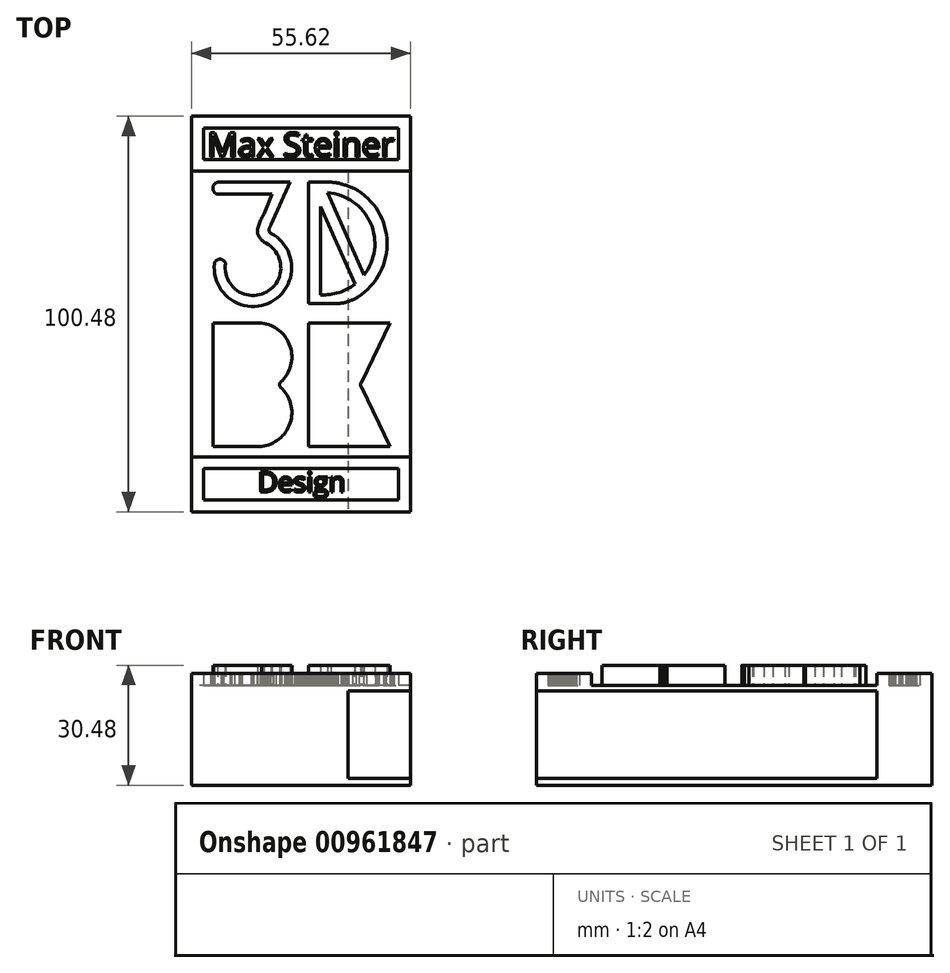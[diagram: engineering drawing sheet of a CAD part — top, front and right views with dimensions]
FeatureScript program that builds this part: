
annotation { "Feature Type Name" : "Feature", "Feature Type Description" : "" }
export const myFeature = defineFeature(function(context is Context, id is Id, definition is map)
    precondition{}
    {
        {
            var Q0;
            Q0=qCreatedBy(makeId("Top.planeOp"),FACE);
            var sketch = newSketch(context, id + "F0", { "sketchPlane" : qUnion([Q0])});
            skLineSegment(sketch, "E0", {"start": v(0, 56.35) * mm, "end": v(0, -56.35) * mm});
            skLineSegment(sketch, "E1", {"start": v(56.35, 0) * mm, "end": v(-56.35, 0) * mm});
            skPoint(sketch, "E2", {"position": v(0, 0) * mm});
            skPoint(sketch, "E3", {"position": v(-22.39, -33.62) * mm});
            skPoint(sketch, "E4", {"position": v(-22.39, 33.48) * mm});
            skPoint(sketch, "E5", {"position": v(21.85, 33.48) * mm});
            skLineSegment(sketch, "E6", {"start": v(1.95, 33.48) * mm, "end": v(7.67, 33.48) * mm});
            skLineSegment(sketch, "E7", {"start": v(21.85, -33.62) * mm, "end": v(1.95, -33.62) * mm});
            skLineSegment(sketch, "E8", {"start": v(21.85, 18.05) * mm, "end": v(21.85, 17.68) * mm});
            skLineSegment(sketch, "E9", {"start": v(-2.74, 33.48) * mm, "end": v(-21.16, 33.48) * mm});
            skLineSegment(sketch, "E10", {"start": v(-22.39, -33.62) * mm, "end": v(-10.07, -33.62) * mm});
            skLineSegment(sketch, "E11", {"start": v(-22.39, -2.3) * mm, "end": v(-22.39, -33.62) * mm});
            skPoint(sketch, "E12", {"position": v(-22.39, 31.95) * mm});
            skPoint(sketch, "E12.positionSnap0", {"position": v(-21.16, 31.95) * mm});
            skArc(sketch, "E13", {"start": v(-21.16, 33.48) * mm, "mid": v(-22.39, 31.95) * mm, "end": v(-21.16, 30.43) * mm});
            skPoint(sketch, "E14", {"position": v(-2.74, 33.48) * mm});
            skPoint(sketch, "E15", {"position": v(-7.3, 30.43) * mm});
            skLineSegment(sketch, "E16", {"start": v(-21.16, 30.43) * mm, "end": v(-7.3, 30.43) * mm});
            skPoint(sketch, "E17", {"position": v(-11.04, 20.68) * mm});
            skPoint(sketch, "E18", {"position": v(-9.45, 18.3) * mm});
            skPoint(sketch, "E19", {"position": v(-9.45, 25.39) * mm});
            skFitSpline(sketch, "E20", {"points": [v(-9.45, 25.39) * mm, v(-11.04, 20.68) * mm, v(-9.45, 18.3) * mm], "startDerivative": vector(-4.65, -9.06) * mm, "endDerivative": vector(5.1, -4.94) * mm});
            skLineSegment(sketch, "E21", {"start": v(-7.3, 30.43) * mm, "end": v(-9.45, 25.39) * mm});
            skPoint(sketch, "E22", {"position": v(-19.2, 12.85) * mm});
            skPoint(sketch, "E23", {"position": v(-12.14, 4.7) * mm});
            skArc(sketch, "E24", {"start": v(-19.2, 12.85) * mm, "mid": v(-8.74, 5.6) * mm, "end": v(-9.45, 18.3) * mm});
            skPoint(sketch, "E25", {"position": v(-8.14, 21.15) * mm});
            skPoint(sketch, "E26", {"position": v(-7.55, 20.43) * mm});
            skPoint(sketch, "E27", {"position": v(-7.55, 22.7) * mm});
            skFitSpline(sketch, "E28", {"points": [v(-7.55, 22.7) * mm, v(-8.14, 21.15) * mm, v(-7.55, 20.43) * mm], "startDerivative": vector(-1.74, -3) * mm, "endDerivative": vector(1.9, -1.47) * mm});
            skLineSegment(sketch, "E29", {"start": v(-2.74, 33.48) * mm, "end": v(-7.55, 22.7) * mm});
            skArc(sketch, "E30.0", {"start": v(-21.98, 12.85) * mm, "mid": v(-7.57, 3.08) * mm, "end": v(-7.62, 20.5) * mm});
            skPoint(sketch, "E31", {"position": v(-21.98, 12.85) * mm});
            skPoint(sketch, "E32", {"position": v(-20.63, 13.93) * mm});
            skArc(sketch, "E33", {"start": v(-19.2, 12.85) * mm, "mid": v(-20.59, 13.94) * mm, "end": v(-21.98, 12.85) * mm});
            skLineSegment(sketch, "E34", {"start": v(1.95, 33.48) * mm, "end": v(1.95, 2.25) * mm});
            skPoint(sketch, "E35", {"position": v(21.85, 18.05) * mm});
            skArc(sketch, "E36", {"start": v(13.56, 3.8) * mm, "mid": v(21.85, 17.87) * mm, "end": v(13.56, 31.93) * mm});
            skPoint(sketch, "E37", {"position": v(7.67, 33.48) * mm});
            skPoint(sketch, "E38", {"position": v(13.56, 31.93) * mm});
            skPoint(sketch, "E39", {"position": v(13.56, 3.8) * mm});
            skArc(sketch, "E40.0", {"start": v(5.03, 4.88) * mm, "mid": v(9.62, 5.44) * mm, "end": v(13.73, 7.58) * mm});
            skLineSegment(sketch, "E40.1", {"start": v(5.03, 27.26) * mm, "end": v(5.03, 4.88) * mm});
            skLineSegment(sketch, "E41", {"start": v(5.03, 27.26) * mm, "end": v(13.73, 7.58) * mm});
            skLineSegment(sketch, "E42", {"start": v(16.04, 9.89) * mm, "end": v(6.78, 30.83) * mm});
            skLineSegment(sketch, "E43", {"start": v(-22.39, -2.3) * mm, "end": v(-10.07, -2.3) * mm});
            skLineSegment(sketch, "E44", {"start": v(1.95, -2.3) * mm, "end": v(1.95, -33.62) * mm});
            skLineSegment(sketch, "E45", {"start": v(1.95, -2.3) * mm, "end": v(22.67, -2.3) * mm});
            skLineSegment(sketch, "E46", {"start": v(22.67, -2.3) * mm, "end": v(15.49, -17.1) * mm});
            skFitSpline(sketch, "E47", {"points": [v(15.49, -17.1) * mm, v(15.2, -17.6) * mm, v(15.17, -17.96) * mm], "startDerivative": vector(-0.63, -0.9) * mm, "endDerivative": vector(0.03, -0.82) * mm});
            skLineSegment(sketch, "E48.MirrorCS", {"start": v(1.95, -33.62) * mm, "end": v(22.67, -33.62) * mm});
            skLineSegment(sketch, "E49.MirrorCS", {"start": v(22.67, -33.62) * mm, "end": v(15.49, -18.82) * mm});
            skFitSpline(sketch, "E50.MirrorCS", {"points": [v(15.49, -18.82) * mm, v(15.2, -18.34) * mm, v(15.17, -17.96) * mm], "startDerivative": vector(-0.63, 0.9) * mm, "endDerivative": vector(0.03, 0.82) * mm});
            skArc(sketch, "E51", {"start": v(-5.17, -17.31) * mm, "mid": v(-2.75, -8.22) * mm, "end": v(-10.07, -2.3) * mm});
            skFitSpline(sketch, "E52", {"points": [v(-5.17, -17.31) * mm, v(-5.38, -17.68) * mm, v(-5.4, -17.96) * mm], "startDerivative": vector(-0.48, -0.68) * mm, "endDerivative": vector(0.02, -0.62) * mm});
            skArc(sketch, "E53.MirrorCS", {"start": v(-5.17, -18.61) * mm, "mid": v(-2.75, -27.7) * mm, "end": v(-10.07, -33.62) * mm});
            skFitSpline(sketch, "E54.MirrorCS", {"points": [v(-5.17, -18.61) * mm, v(-5.38, -18.25) * mm, v(-5.4, -17.96) * mm], "startDerivative": vector(-0.48, 0.68) * mm, "endDerivative": vector(0.02, 0.62) * mm});
            skPoint(sketch, "E55.end.orphan", {"position": v(-10.07, -33.62) * mm});
            skPoint(sketch, "E56.orphan", {"position": v(-10.07, -17.96) * mm});
            skPoint(sketch, "E57.orphan", {"position": v(0, -33.62) * mm});
            skLineSegment(sketch, "E58.MirrorCS", {"start": v(0, 2.62) * mm, "end": v(7.67, 2.62) * mm});
            skArc(sketch, "E59.trimOffspring", {"start": v(16.04, 9.89) * mm, "mid": v(17.67, 23.12) * mm, "end": v(6.78, 30.83) * mm});
            skPoint(sketch, "E60", {"position": v(7.67, 2.62) * mm});
            skFitSpline(sketch, "E61", {"points": [v(13.56, 3.8) * mm, v(10.55, 2.81) * mm, v(7.67, 2.62) * mm], "startDerivative": vector(-5.9, -2.33) * mm, "endDerivative": vector(-5.9, -0.02) * mm});
            skPoint(sketch, "E62.1.internal.snap0", {"position": v(9.38, 17.42) * mm});
            skFitSpline(sketch, "E62", {"points": [v(13.56, 31.93) * mm, v(9.38, 33.27) * mm, v(7.67, 33.48) * mm], "startDerivative": vector(-7.54, 2.7) * mm, "endDerivative": vector(-3.99, 0.22) * mm});
            skPoint(sketch, "E63.orphan", {"position": v(10.87, 2.62) * mm});
            skPoint(sketch, "E64.orphan", {"position": v(0, 33.48) * mm});
            skPoint(sketch, "E65.trimOffspring.start.orphan", {"position": v(21.85, 2.62) * mm});
            skLineSegment(sketch, "E66", {"start": v(-27.8, 0) * mm, "end": v(-27.8, 46.45) * mm});
            skLineSegment(sketch, "E67", {"start": v(-27.8, 46.45) * mm, "end": v(0, 46.45) * mm});
            skLineSegment(sketch, "E68.MirrorCS", {"start": v(27.8, 0) * mm, "end": v(27.8, 46.45) * mm});
            skLineSegment(sketch, "E69.MirrorCS", {"start": v(-27.8, -46.45) * mm, "end": v(0, -46.45) * mm});
            skLineSegment(sketch, "E70.MirrorCS", {"start": v(-27.8, 0) * mm, "end": v(-27.8, -46.45) * mm});
            skLineSegment(sketch, "E71.MirrorCS", {"start": v(27.8, 46.45) * mm, "end": v(0, 46.45) * mm});
            skLineSegment(sketch, "E72.MirrorCS", {"start": v(27.8, 0) * mm, "end": v(27.8, -46.45) * mm});
            skLineSegment(sketch, "E73.MirrorCS", {"start": v(27.8, -46.45) * mm, "end": v(0, -46.45) * mm});
            skSolve(sketch);
        }
        {
            var Q0;
            Q0=qCreatedBy(makeId("Top.planeOp"),FACE);
            var sketch = newSketch(context, id + "F1", { "sketchPlane" : qUnion([Q0])});
            skLineSegment(sketch, "E74.bottom", {"start": v(-27.8, 46.45) * mm, "end": v(27.8, 46.45) * mm});
            skLineSegment(sketch, "E74.top", {"start": v(-27.8, -46.45) * mm, "end": v(27.8, -46.45) * mm});
            skLineSegment(sketch, "E74.left", {"start": v(-27.8, 46.45) * mm, "end": v(-27.8, -46.45) * mm});
            skLineSegment(sketch, "E74.right", {"start": v(27.8, 46.45) * mm, "end": v(27.8, -46.45) * mm});
            skSolve(sketch);
        }
        {
            var Q0;
            Q0=makeQuery(id+"F1.imprint","IMPRINT",FACE,{"disambiguationData":[TD([[makeQuery(id+"F1.imprint","IMPRINT",EDGE,{"derivedFrom":sQuery(id+"F1.wireOp",EDGE,"E74.bottom")}),-1.0]])]});
            extrude(context, id + "F2", {"entities" : qUnion([Q0]), "oppositeDirection" : true, "depth" : 25.4 * mm, "offsetDistance" : 25.4 * mm});
        }
        {
            var Q0;
            {var subQ7=sQuery(id+"F0.wireOp",EDGE,"E6");Q0=makeQuery(id+"F0.imprint","IMPRINT",FACE,{"disambiguationData":[TD([[makeQuery(id+"F0.imprint","IMPRINT",EDGE,{"derivedFrom":subQ7}),-1.0]])]});}
            var Q1;
            Q1=makeQuery(id+"F0.imprint","IMPRINT",FACE,{"disambiguationData":[TD([[makeQuery(id+"F0.imprint","IMPRINT",EDGE,{"derivedFrom":sQuery(id+"F0.wireOp",EDGE,"E9")}),1.0]])]});
            var Q2;
            {var subQ0=sQuery(id+"F0.wireOp",EDGE,"E44");Q2=makeQuery(id+"F0.imprint","IMPRINT",FACE,{"disambiguationData":[TD([[makeQuery(id+"F0.imprint","IMPRINT",EDGE,{"derivedFrom":subQ0}),1.0]])]});}
            var Q3;
            Q3=makeQuery(id+"F0.imprint","IMPRINT",FACE,{"disambiguationData":[TD([[makeQuery(id+"F0.imprint","IMPRINT",EDGE,{"derivedFrom":sQuery(id+"F0.wireOp",EDGE,"E10")}),1.0]])]});
            extrude(context, id + "F3", {"entities" : qUnion([Q0, Q1, Q2, Q3]), "operationType" : NewBodyOperationType.ADD, "depth" : 5.08 * mm, "offsetDistance" : 25.4 * mm});
        }
        {
            var Q0;
            {var subQ3=sQuery(id+"F1.wireOp",EDGE,"E74.bottom");var subQ5=sQuery(id+"F1.wireOp",EDGE,"E74.left");var subQ6=sQuery(id+"F1.wireOp",EDGE,"E74.top");var subQ7=sQuery(id+"F1.wireOp",EDGE,"E74.right");Q0=makeQuery(id+"F3.boolean.opBoolean","SPLIT",FACE,{"disambiguationData":[TD([makeQuery(id+"F2.opExtrude","SWEPT_FACE",FACE,{"disambiguationData":[OSD([subQ3])]})])],"derivedFrom":makeQuery(id+"F2.opExtrude","CAP_FACE",FACE,{"disambiguationData":[OSD([subQ3,subQ6,subQ5,subQ7])],"isStart":true})});}
            var sketch = newSketch(context, id + "F4", { "sketchPlane" : qUnion([Q0])});
            skLineSegment(sketch, "E75", {"start": v(-27.8, 36.27) * mm, "end": v(27.8, 36.27) * mm});
            skLineSegment(sketch, "E76", {"start": v(-27.8, 36.27) * mm, "end": v(-27.8, 50.24) * mm});
            skLineSegment(sketch, "E77", {"start": v(-27.8, 50.24) * mm, "end": v(27.8, 50.24) * mm});
            skLineSegment(sketch, "E78", {"start": v(27.8, 50.24) * mm, "end": v(27.8, 36.27) * mm});
            skLineSegment(sketch, "E79.0", {"start": v(-24.8, 47.24) * mm, "end": v(24.8, 47.24) * mm});
            skLineSegment(sketch, "E79.1", {"start": v(-24.8, 39.27) * mm, "end": v(-24.8, 47.24) * mm});
            skLineSegment(sketch, "E79.2", {"start": v(-24.8, 39.27) * mm, "end": v(24.8, 39.27) * mm});
            skLineSegment(sketch, "E79.3", {"start": v(24.8, 47.24) * mm, "end": v(24.8, 39.27) * mm});
            skText(sketch, "E80", { "text": "Max Steiner", "fontName": "OpenSans-Regular.ttf"});
            skLineSegment(sketch, "E81", {"start": v(0, 0) * mm, "end": v(41.07, 0) * mm});
            skLineSegment(sketch, "E82.MirrorCS", {"start": v(-27.8, -50.24) * mm, "end": v(27.8, -50.24) * mm});
            skLineSegment(sketch, "E83.MirrorCS", {"start": v(-27.8, -36.27) * mm, "end": v(-27.8, -50.24) * mm});
            skLineSegment(sketch, "E84.MirrorCS", {"start": v(27.8, -50.24) * mm, "end": v(27.8, -36.27) * mm});
            skLineSegment(sketch, "E85.MirrorCS", {"start": v(-24.8, -39.27) * mm, "end": v(24.8, -39.27) * mm});
            skLineSegment(sketch, "E86.MirrorCS", {"start": v(-24.8, -39.27) * mm, "end": v(-24.8, -47.24) * mm});
            skLineSegment(sketch, "E87.MirrorCS", {"start": v(-24.8, -47.24) * mm, "end": v(24.8, -47.24) * mm});
            skLineSegment(sketch, "E88.MirrorCS", {"start": v(24.8, -47.24) * mm, "end": v(24.8, -39.27) * mm});
            skText(sketch, "E89", { "text": "Design", "fontName": "OpenSans-Regular.ttf"});
            skPoint(sketch, "E90", {"position": v(0, -39.27) * mm});
            skPoint(sketch, "E91", {"position": v(24.8, -43.26) * mm});
            skLineSegment(sketch, "E92", {"start": v(27.8, -36.27) * mm, "end": v(-27.8, -36.27) * mm});
            const initialGuessF4  = {"E80": [-0.02384, 0.03994, 1, 0, 0.00618], "E89": [-0.011, -0.04517, 1, 0, 0.00504]};
            skSetInitialGuess(sketch, initialGuessF4);
            skSolve(sketch);
        }
        {
            var Q0;
            Q0=makeQuery(id+"F4.imprint","IMPRINT",FACE,{"disambiguationData":[TD([[makeQuery(id+"F4.imprint","IMPRINT",EDGE,{"derivedFrom":sQuery(id+"F4.wireOp",EDGE,"E80.sketch_text.stroke-18")}),-1.0]])]});
            var Q1;
            Q1=makeQuery(id+"F4.imprint","IMPRINT",FACE,{"disambiguationData":[TD([[makeQuery(id+"F4.imprint","IMPRINT",EDGE,{"derivedFrom":sQuery(id+"F4.wireOp",EDGE,"E80.sketch_text.stroke-0")}),-1.0]])]});
            var Q2;
            Q2=makeQuery(id+"F4.imprint","IMPRINT",FACE,{"disambiguationData":[TD([[makeQuery(id+"F4.imprint","IMPRINT",EDGE,{"derivedFrom":sQuery(id+"F4.wireOp",EDGE,"E80.sketch_text.stroke-45")}),-1.0]])]});
            var Q3;
            Q3=makeQuery(id+"F4.imprint","IMPRINT",FACE,{"disambiguationData":[TD([[makeQuery(id+"F4.imprint","IMPRINT",EDGE,{"derivedFrom":sQuery(id+"F4.wireOp",EDGE,"E80.sketch_text.stroke-57")}),-1.0]])]});
            var Q4;
            Q4=makeQuery(id+"F4.imprint","IMPRINT",FACE,{"disambiguationData":[TD([[makeQuery(id+"F4.imprint","IMPRINT",EDGE,{"derivedFrom":sQuery(id+"F4.wireOp",EDGE,"E80.sketch_text.stroke-82")}),-1.0]])]});
            var Q5;
            Q5=makeQuery(id+"F4.imprint","IMPRINT",FACE,{"disambiguationData":[TD([[makeQuery(id+"F4.imprint","IMPRINT",EDGE,{"derivedFrom":sQuery(id+"F4.wireOp",EDGE,"E80.sketch_text.stroke-101")}),-1.0]])]});
            var Q6;
            Q6=makeQuery(id+"F4.imprint","IMPRINT",FACE,{"disambiguationData":[TD([[makeQuery(id+"F4.imprint","IMPRINT",EDGE,{"derivedFrom":sQuery(id+"F4.wireOp",EDGE,"E80.sketch_text.stroke-120")}),-1.0]])]});
            var Q7;
            Q7=makeQuery(id+"F4.imprint","IMPRINT",FACE,{"disambiguationData":[TD([[makeQuery(id+"F4.imprint","IMPRINT",EDGE,{"derivedFrom":sQuery(id+"F4.wireOp",EDGE,"E80.sketch_text.stroke-124")}),-1.0]])]});
            var Q8;
            Q8=makeQuery(id+"F4.imprint","IMPRINT",FACE,{"disambiguationData":[TD([[makeQuery(id+"F4.imprint","IMPRINT",EDGE,{"derivedFrom":sQuery(id+"F4.wireOp",EDGE,"E80.sketch_text.stroke-132")}),-1.0]])]});
            var Q9;
            Q9=makeQuery(id+"F4.imprint","IMPRINT",FACE,{"disambiguationData":[TD([[makeQuery(id+"F4.imprint","IMPRINT",EDGE,{"derivedFrom":sQuery(id+"F4.wireOp",EDGE,"E80.sketch_text.stroke-149")}),-1.0]])]});
            var Q10;
            Q10=makeQuery(id+"F4.imprint","IMPRINT",FACE,{"disambiguationData":[TD([[makeQuery(id+"F4.imprint","IMPRINT",EDGE,{"derivedFrom":sQuery(id+"F4.wireOp",EDGE,"E80.sketch_text.stroke-168")}),-1.0]])]});
            var Q11;
            {var subQ0=sQuery(id+"F4.wireOp",EDGE,"E76");Q11=makeQuery(id+"F4.imprint","IMPRINT",FACE,{"disambiguationData":[TD([[makeQuery(id+"F4.imprint","IMPRINT",EDGE,{"derivedFrom":subQ0}),1.0]])]});}
            var Q12;
            {var subQ2=sQuery(id+"F4.wireOp",EDGE,"E77");Q12=makeQuery(id+"F4.imprint","IMPRINT",FACE,{"disambiguationData":[TD([[makeQuery(id+"F4.imprint","IMPRINT",EDGE,{"derivedFrom":subQ2}),-1.0]])]});}
            extrude(context, id + "F5", {"entities" : qUnion([Q0, Q1, Q2, Q3, Q4, Q5, Q6, Q7, Q8, Q9, Q10, Q11, Q12]), "operationType" : NewBodyOperationType.ADD, "depth" : 3 * mm, "offsetDistance" : 25.4 * mm});
        }
        {
            var Q0;
            {var subQ1=sQuery(id+"F4.wireOp",EDGE,"E85.MirrorCS");Q0=makeQuery(id+"F4.imprint","IMPRINT",FACE,{"disambiguationData":[TD([[makeQuery(id+"F4.imprint","IMPRINT",EDGE,{"derivedFrom":subQ1}),1.0]])]});}
            var Q1;
            {var subQ8=sQuery(id+"F4.wireOp",EDGE,"E82.MirrorCS");Q1=makeQuery(id+"F4.imprint","IMPRINT",FACE,{"disambiguationData":[TD([[makeQuery(id+"F4.imprint","IMPRINT",EDGE,{"derivedFrom":subQ8}),1.0]])]});}
            var Q2;
            Q2=makeQuery(id+"F4.imprint","IMPRINT",FACE,{"disambiguationData":[TD([[makeQuery(id+"F4.imprint","IMPRINT",EDGE,{"derivedFrom":sQuery(id+"F4.wireOp",EDGE,"E89.sketch_text.stroke-0")}),-1.0]])]});
            var Q3;
            Q3=makeQuery(id+"F4.imprint","IMPRINT",FACE,{"disambiguationData":[TD([[makeQuery(id+"F4.imprint","IMPRINT",EDGE,{"derivedFrom":sQuery(id+"F4.wireOp",EDGE,"E89.sketch_text.stroke-14")}),-1.0]])]});
            var Q4;
            Q4=makeQuery(id+"F4.imprint","IMPRINT",FACE,{"disambiguationData":[TD([[makeQuery(id+"F4.imprint","IMPRINT",EDGE,{"derivedFrom":sQuery(id+"F4.wireOp",EDGE,"E89.sketch_text.stroke-33")}),-1.0]])]});
            var Q5;
            Q5=makeQuery(id+"F4.imprint","IMPRINT",FACE,{"disambiguationData":[TD([[makeQuery(id+"F4.imprint","IMPRINT",EDGE,{"derivedFrom":sQuery(id+"F4.wireOp",EDGE,"E89.sketch_text.stroke-58")}),-1.0]])]});
            var Q6;
            Q6=makeQuery(id+"F4.imprint","IMPRINT",FACE,{"disambiguationData":[TD([[makeQuery(id+"F4.imprint","IMPRINT",EDGE,{"derivedFrom":sQuery(id+"F4.wireOp",EDGE,"E89.sketch_text.stroke-62")}),-1.0]])]});
            var Q7;
            Q7=makeQuery(id+"F4.imprint","IMPRINT",FACE,{"disambiguationData":[TD([[makeQuery(id+"F4.imprint","IMPRINT",EDGE,{"derivedFrom":sQuery(id+"F4.wireOp",EDGE,"E89.sketch_text.stroke-114")}),-1.0]])]});
            var Q8;
            Q8=makeQuery(id+"F4.imprint","IMPRINT",FACE,{"disambiguationData":[TD([[makeQuery(id+"F4.imprint","IMPRINT",EDGE,{"derivedFrom":sQuery(id+"F4.wireOp",EDGE,"E89.sketch_text.stroke-70")}),-1.0]])]});
            var Q9;
            {var subQ6=sQuery(id+"F4.wireOp",EDGE,"E89.sketch_text.stroke-84");Q9=makeQuery(id+"F4.imprint","IMPRINT",FACE,{"disambiguationData":[TD([[makeQuery(id+"F4.imprint","IMPRINT",EDGE,{"derivedFrom":subQ6}),-1.0]])]});}
            extrude(context, id + "F6", {"entities" : qUnion([Q0, Q1, Q2, Q3, Q4, Q5, Q6, Q7, Q8, Q9]), "operationType" : NewBodyOperationType.ADD, "depth" : 3 * mm, "offsetDistance" : 25.4 * mm});
        }
        {
            var Q0;
            Q0=makeQuery(id+"F5.opExtrude","CAP_FACE",FACE,{"disambiguationData":[OSD([sQuery(id+"F4.wireOp",EDGE,"E75"),sQuery(id+"F4.wireOp",EDGE,"E76"),sQuery(id+"F4.wireOp",EDGE,"E77"),sQuery(id+"F4.wireOp",EDGE,"E78"),sQuery(id+"F4.wireOp",EDGE,"E79.0"),sQuery(id+"F4.wireOp",EDGE,"E79.1"),sQuery(id+"F4.wireOp",EDGE,"E79.2"),sQuery(id+"F4.wireOp",EDGE,"E79.3")])],"isStart":true});
            var sketch = newSketch(context, id + "F7", { "sketchPlane" : qUnion([Q0])});
            skLineSegment(sketch, "E93.bottom", {"start": v(27.8, -50.24) * mm, "end": v(-27.8, -50.24) * mm});
            skLineSegment(sketch, "E93.top", {"start": v(27.8, -46.45) * mm, "end": v(-27.8, -46.45) * mm});
            skLineSegment(sketch, "E93.left", {"start": v(27.8, -50.24) * mm, "end": v(27.8, -46.45) * mm});
            skLineSegment(sketch, "E93.right", {"start": v(-27.8, -50.24) * mm, "end": v(-27.8, -46.45) * mm});
            skSolve(sketch);
        }
        {
            var Q0;
            Q0 = qSketchRegion(id + "F7", true);
            var Q1;
            Q1=makeQuery(id+"F2.opExtrude","CAP_FACE",FACE,{"disambiguationData":[OSD([sQuery(id+"F1.wireOp",EDGE,"E74.bottom"),sQuery(id+"F1.wireOp",EDGE,"E74.top"),sQuery(id+"F1.wireOp",EDGE,"E74.left"),sQuery(id+"F1.wireOp",EDGE,"E74.right")])],"isStart":false});
            extrude(context, id + "F8", {"entities" : qUnion([Q0]), "operationType" : NewBodyOperationType.ADD, "endBound" : BoundingType.UP_TO_SURFACE, "depth" : 25.4 * mm, "endBoundEntityFace" : qUnion([Q1]), "offsetDistance" : 25.4 * mm});
        }
        {
            var Q0;
            Q0=makeQuery(id+"F6.opExtrude","CAP_FACE",FACE,{"disambiguationData":[OSD([sQuery(id+"F4.wireOp",EDGE,"E82.MirrorCS"),sQuery(id+"F4.wireOp",EDGE,"E83.MirrorCS"),sQuery(id+"F4.wireOp",EDGE,"E84.MirrorCS"),sQuery(id+"F4.wireOp",EDGE,"E85.MirrorCS"),sQuery(id+"F4.wireOp",EDGE,"E86.MirrorCS"),sQuery(id+"F4.wireOp",EDGE,"E87.MirrorCS"),sQuery(id+"F4.wireOp",EDGE,"E88.MirrorCS"),sQuery(id+"F4.wireOp",EDGE,"E92")])],"isStart":true});
            var sketch = newSketch(context, id + "F9", { "sketchPlane" : qUnion([Q0])});
            skLineSegment(sketch, "E94.bottom", {"start": v(-27.8, 50.24) * mm, "end": v(27.8, 50.24) * mm});
            skLineSegment(sketch, "E94.top", {"start": v(-27.8, 46.45) * mm, "end": v(27.8, 46.45) * mm});
            skLineSegment(sketch, "E94.left", {"start": v(-27.8, 50.24) * mm, "end": v(-27.8, 46.45) * mm});
            skLineSegment(sketch, "E94.right", {"start": v(27.8, 50.24) * mm, "end": v(27.8, 46.45) * mm});
            skSolve(sketch);
        }
        {
            var Q0;
            Q0 = qSketchRegion(id + "F9", true);
            var Q1;
            Q1=makeQuery(id+"F8.boolean.opBoolean","MERGE",FACE,{"derivedFrom":[makeQuery(id+"F2.opExtrude","CAP_FACE",FACE,{"disambiguationData":[OSD([sQuery(id+"F1.wireOp",EDGE,"E74.bottom"),sQuery(id+"F1.wireOp",EDGE,"E74.top"),sQuery(id+"F1.wireOp",EDGE,"E74.left"),sQuery(id+"F1.wireOp",EDGE,"E74.right")])],"isStart":false}),makeQuery(id+"F8.opExtrude","CAP_FACE",FACE,{"disambiguationData":[OSD([sQuery(id+"F7.wireOp",EDGE,"E93.bottom"),sQuery(id+"F7.wireOp",EDGE,"E93.top"),sQuery(id+"F7.wireOp",EDGE,"E93.left"),sQuery(id+"F7.wireOp",EDGE,"E93.right")])],"isStart":false})]});
            extrude(context, id + "F10", {"entities" : qUnion([Q0]), "operationType" : NewBodyOperationType.ADD, "endBound" : BoundingType.UP_TO_SURFACE, "depth" : 25.4 * mm, "endBoundEntityFace" : qUnion([Q1]), "offsetDistance" : 25.4 * mm});
        }
        {
            var Q0;
            Q0=makeQuery(id+"F10.boolean.opBoolean","MERGE",FACE,{"derivedFrom":[makeQuery(id+"F6.opExtrude","SWEPT_FACE",FACE,{"disambiguationData":[OSD([sQuery(id+"F4.wireOp",EDGE,"E82.MirrorCS")])]}),makeQuery(id+"F10.opExtrude","SWEPT_FACE",FACE,{"disambiguationData":[OSD([sQuery(id+"F9.wireOp",EDGE,"E94.bottom")])]})]});
            var sketch = newSketch(context, id + "F11", { "sketchPlane" : qUnion([Q0])});
            skLineSegment(sketch, "E95", {"start": v(-27.8, 0) * mm, "end": v(27.8, 0) * mm});
            skPoint(sketch, "E96", {"position": v(27.8, 0) * mm});
            skPoint(sketch, "E97", {"position": v(27.8, -25.4) * mm});
            skLineSegment(sketch, "E98", {"start": v(27.8, -9.42) * mm, "end": v(11.93, -9.42) * mm});
            skLineSegment(sketch, "E99", {"start": v(11.93, -9.42) * mm, "end": v(11.93, -1.48) * mm});
            skLineSegment(sketch, "E100", {"start": v(11.93, -1.48) * mm, "end": v(27.8, -1.48) * mm});
            skLineSegment(sketch, "E101", {"start": v(27.8, -1.48) * mm, "end": v(27.8, -9.42) * mm});
            skLineSegment(sketch, "E102.MirrorCS", {"start": v(11.93, -17.36) * mm, "end": v(27.8, -17.36) * mm});
            skLineSegment(sketch, "E103.MirrorCS", {"start": v(11.93, -9.42) * mm, "end": v(11.93, -17.36) * mm});
            skLineSegment(sketch, "E104", {"start": v(11.93, -17.36) * mm, "end": v(11.93, -21.17) * mm});
            skLineSegment(sketch, "E105", {"start": v(11.93, -21.17) * mm, "end": v(27.8, -21.17) * mm});
            skLineSegment(sketch, "E106", {"start": v(11.93, -21.17) * mm, "end": v(11.93, -22.44) * mm});
            skLineSegment(sketch, "E107", {"start": v(11.93, -22.44) * mm, "end": v(11.93, -23.7) * mm});
            skLineSegment(sketch, "E108", {"start": v(11.93, -23.7) * mm, "end": v(27.8, -23.7) * mm});
            skSolve(sketch);
        }
        {
            var Q0;
            Q0=makeQuery(id+"F11.imprint","IMPRINT",FACE,{"disambiguationData":[TD([[makeQuery(id+"F11.imprint","IMPRINT",EDGE,{"derivedFrom":sQuery(id+"F11.wireOp",EDGE,"E98")}),-1.0]])]});
            var Q1;
            {var subQ0=sQuery(id+"F11.wireOp",EDGE,"E98");Q1=makeQuery(id+"F11.imprint","IMPRINT",FACE,{"disambiguationData":[TD([[makeQuery(id+"F11.imprint","IMPRINT",EDGE,{"derivedFrom":subQ0}),1.0]])]});}
            var Q2;
            {var subQ0=sQuery(id+"F11.wireOp",EDGE,"E102.MirrorCS");Q2=makeQuery(id+"F11.imprint","IMPRINT",FACE,{"disambiguationData":[TD([[makeQuery(id+"F11.imprint","IMPRINT",EDGE,{"derivedFrom":subQ0}),-1.0]])]});}
            var Q3;
            {var subQ1=sQuery(id+"F11.wireOp",EDGE,"E105");Q3=makeQuery(id+"F11.imprint","IMPRINT",FACE,{"disambiguationData":[TD([[makeQuery(id+"F11.imprint","IMPRINT",EDGE,{"derivedFrom":subQ1}),-1.0]])]});}
            var Q4;
            Q4=makeQuery(id+"F5.opExtrude","SWEPT_FACE",FACE,{"disambiguationData":[OSD([sQuery(id+"F4.wireOp",EDGE,"E75")])]});
            extrude(context, id + "F12", {"entities" : qUnion([Q0, Q1, Q2, Q3]), "operationType" : NewBodyOperationType.REMOVE, "endBound" : BoundingType.UP_TO_SURFACE, "oppositeDirection" : true, "depth" : 25.4 * mm, "endBoundEntityFace" : qUnion([Q4]), "offsetDistance" : 25.4 * mm});
        }
    });
